# Revit family: BasinMixer-Vitra-İstanbulSeries-A41826
name_source: partatom
category: Plumbing Fixtures
revit_build: Autodesk Revit 2017 (Build: 20160225_1515(x64)
units: mm (PartAtom-declared; Revit-internal decimal feet)

## family parameters
Cut with Voids When Loaded = No
Host = Face
OmniClass Number = 23.45.55.17
OmniClass Title = Mixing Faucets
Part Type = Normal
Room Calculation Point = No
Round Connector Dimension = Use Diameter
Shared = Yes

## types (10) — shared parameters
BIMobject category = Taps & Mixers
Brand = VitrA
CW Connection = Yes
Coating Material = Chrome
Default Elevation = 850 mm
Description = Istanbul Basin Mixer
Design country = Turkey
HW Connection = Yes
Hot Water Supply (max.) = 80 °C
Hot Water temperature, factory set to = 38 °C
IFC Classification = Sanitary Terminal
Installation instructions = https://cdn.vitra.com.tr
Main Material = Brass
Manufacturer = Vitra
Manufacturer name = Vitra
Masterformat 2014 Code = 22 40 00
Masterformat 2014 Description = Plumbing Fixtures
Min. flow pressure of = 0.5 bar
Mounting type = Countertop
NBS Referans Code = 45-35-70/371
NBS Referans Description = Water supply fittings for wash basins and troughs
Nominal Depth (mm) = 182 mm
Nominal Height (mm) = 148 mm
Nominal Width (mm) = 125 mm
Number Of Connections = 2
OmniClass Code = 23.45.55.17
OmniClass Description = Mixing Faucets
Primary Material = <By Category>
Product Guid = https://cdn.vitra.com.tr
Product Properties = Extra Water Saving, Green Building Certification
Product Type = Basin Mixer
Product certification = https://www.vitraglobal.com
Product family = İstanbul
Product group = İstanbul Basin Mixer
Range of Hot Water Supply = 5 - 65 °C
Range of flow pressure = 1 - 5 bar
Test Pressure = 16 bar
URL = https://vitraglobal.com
Uniclass 1.4 Code = L725111
Uniclass 1.4 Description = Mixer taps
Uniclass 2.0 Code = Pr_40_30_96_98
Uniclass 2.0 Description = Washbasin Tap
Uniclass 2015 Code = Pr_40_20_87_98
Uniclass 2015 Name = Washbasin Tap
Uniformat II Code = 22 40 00
Uniformat II Description = Plumbing Fixture
Vent Connection = No
Waste Connection = No
Weight Net (kg) = 2.75
Youtube = https://www.youtube.com

## per-type parameters (varying)
| type | Article No. (default) | Color | Connection Diameter (mm) | Flow Rate(L/min. - 3 bar) | Model | Product SKU | Product data url | Technical description | Warranty Period (Year) |
| BasinMixer-Vitra-İstanbulSeries-A41826VUK | A41826VUK | Chrome | 15 mm | 3 L/min. | A41826VUK | A41826VUK | https://www.vitraglobal.com | https://www.vitraglobal.com | 7 Years |
| BasinMixer-Vitra-İstanbulSeries-A4182699EXP | A4182699EXP | White | 10 mm  [stored 0.0328084 ft] | 5 L/min. | A4182699EXP | A4182699EXP | https://www.vitra.com.tr | https://www.vitra.com.tr | 7 Years |
| BasinMixer-Vitra-İstanbulSeries-A4182699 | A4182699 | White | 10 mm  [stored 0.0328084 ft] | 5 L/min. | A4182699 | A4182699 | https://www.vitra.com.tr | https://www.vitra.com.tr | 10 Years |
| BasinMixer-Vitra-İstanbulSeries-A4182692EXP | A4182692EXP | Black | 10 mm  [stored 0.0328084 ft] | 3 L/min. | A4182692EXP | A4182692EXP | https://www.vitra.com.tr | https://www.vitra.com.tr | 7 Years |
| BasinMixer-Vitra-İstanbulSeries-A4182692 | A4182692 | Black | 10 mm  [stored 0.0328084 ft] | 5 L/min. | A4182692 | A4182692 | https://www.vitra.com.tr | https://www.vitra.com.tr | 10 Years |
| BasinMixer-Vitra-İstanbulSeries-A4182623VUK | A4182623VUK | Gold | 15 mm | 3 L/min. | A4182623VUK | A4182623VUK | https://www.vitraglobal.com | https://www.vitraglobal.com | 7 Years |
| BasinMixer-Vitra-İstanbulSeries-A4182623 | A4182623 | Gold | 10 mm  [stored 0.0328084 ft] | 5 L/min. | A4182623 | A4182623 | https://www.vitra.com.tr | https://www.vitra.com.tr | 10 Years |
| BasinMixer-Vitra-İstanbulSeries-A41826EXP | A41826EXP | Chrome | 10 mm  [stored 0.0328084 ft] | 3 L/min. | A41826EXP | A41826EXP | https://www.vitraglobal.com | https://www.vitraglobal.com | 7 Years |
| BasinMixer-Vitra-İstanbulSeries-A4182623EXP | A4182623EXP | Gold | 10 mm  [stored 0.0328084 ft] | 3 L/min. | A4182623EXP | A4182623EXP | https://www.vitraglobal.com | https://www.vitraglobal.com | 7 Years |
| BasinMixer-Vitra-İstanbulSeries-A41826 | A41826 | Chrome | 10 mm  [stored 0.0328084 ft] | 5 L/min. | A41826 | A41826 | https://www.vitra.com.tr | https://www.vitra.com.tr | 10 Years |

note: [stored X ft] marks values corroborated as IEEE doubles in the binary element streams (Revit-internal decimal feet)

## geometry (parser evidence)
native form markers: Sweep x3
no freeform markers — native parametric forms only
